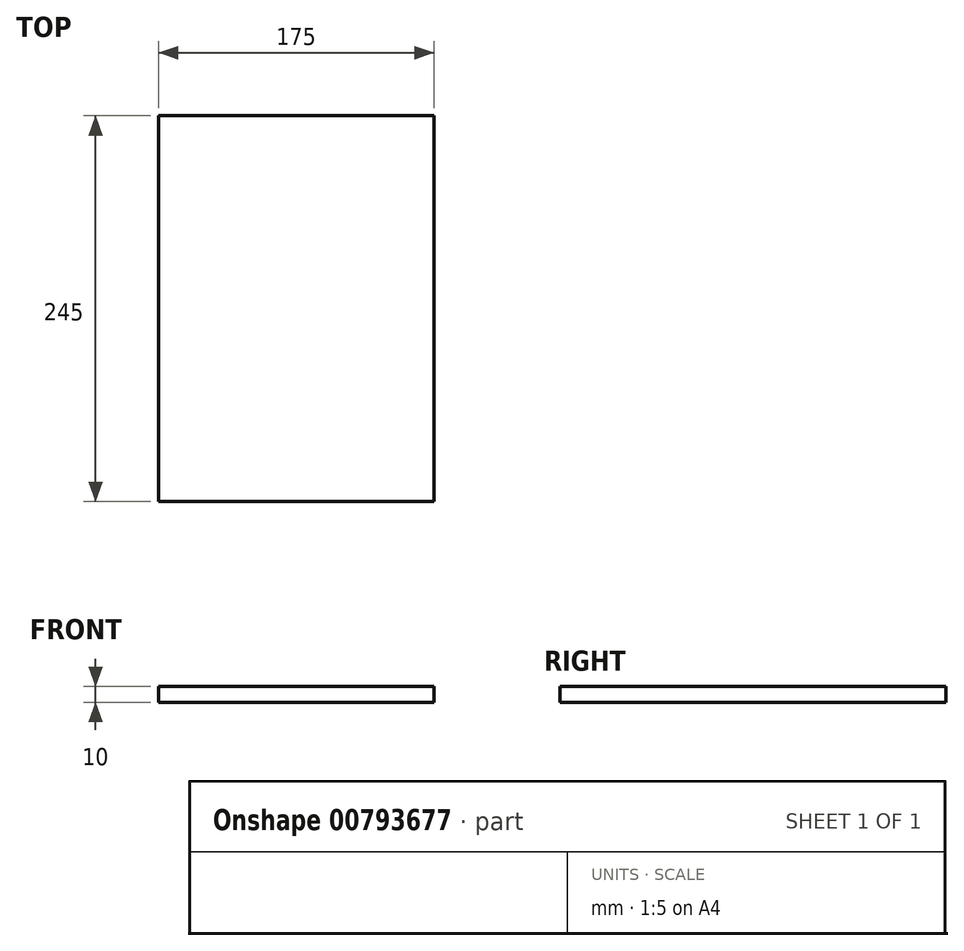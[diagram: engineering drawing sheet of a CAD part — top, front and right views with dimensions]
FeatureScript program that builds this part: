
annotation { "Feature Type Name" : "Feature", "Feature Type Description" : "" }
export const myFeature = defineFeature(function(context is Context, id is Id, definition is map)
    precondition{}
    {
        {
            var Q0;
            Q0=qCreatedBy(makeId("Top.planeOp"),FACE);
            var sketch = newSketch(context, id + "F0", { "sketchPlane" : qUnion([Q0])});
            skLineSegment(sketch, "E0.bottom", {"start": v(0, 0) * mm, "end": v(175, 0) * mm});
            skLineSegment(sketch, "E0.top", {"start": v(0, 245) * mm, "end": v(175, 245) * mm});
            skLineSegment(sketch, "E0.left", {"start": v(0, 0) * mm, "end": v(0, 245) * mm});
            skLineSegment(sketch, "E0.right", {"start": v(175, 0) * mm, "end": v(175, 245) * mm});
            skSolve(sketch);
        }
        {
            var Q0;
            Q0=makeQuery(id+"F0.imprint","IMPRINT",FACE,{"disambiguationData":[TD([[makeQuery(id+"F0.imprint","IMPRINT",EDGE,{"derivedFrom":sQuery(id+"F0.wireOp",EDGE,"E0.bottom")}),1.0]])]});
            extrude(context, id + "F1", {"entities" : qUnion([Q0]), "depth" : 10 * mm, "offsetDistance" : 25 * mm});
        }
    });
